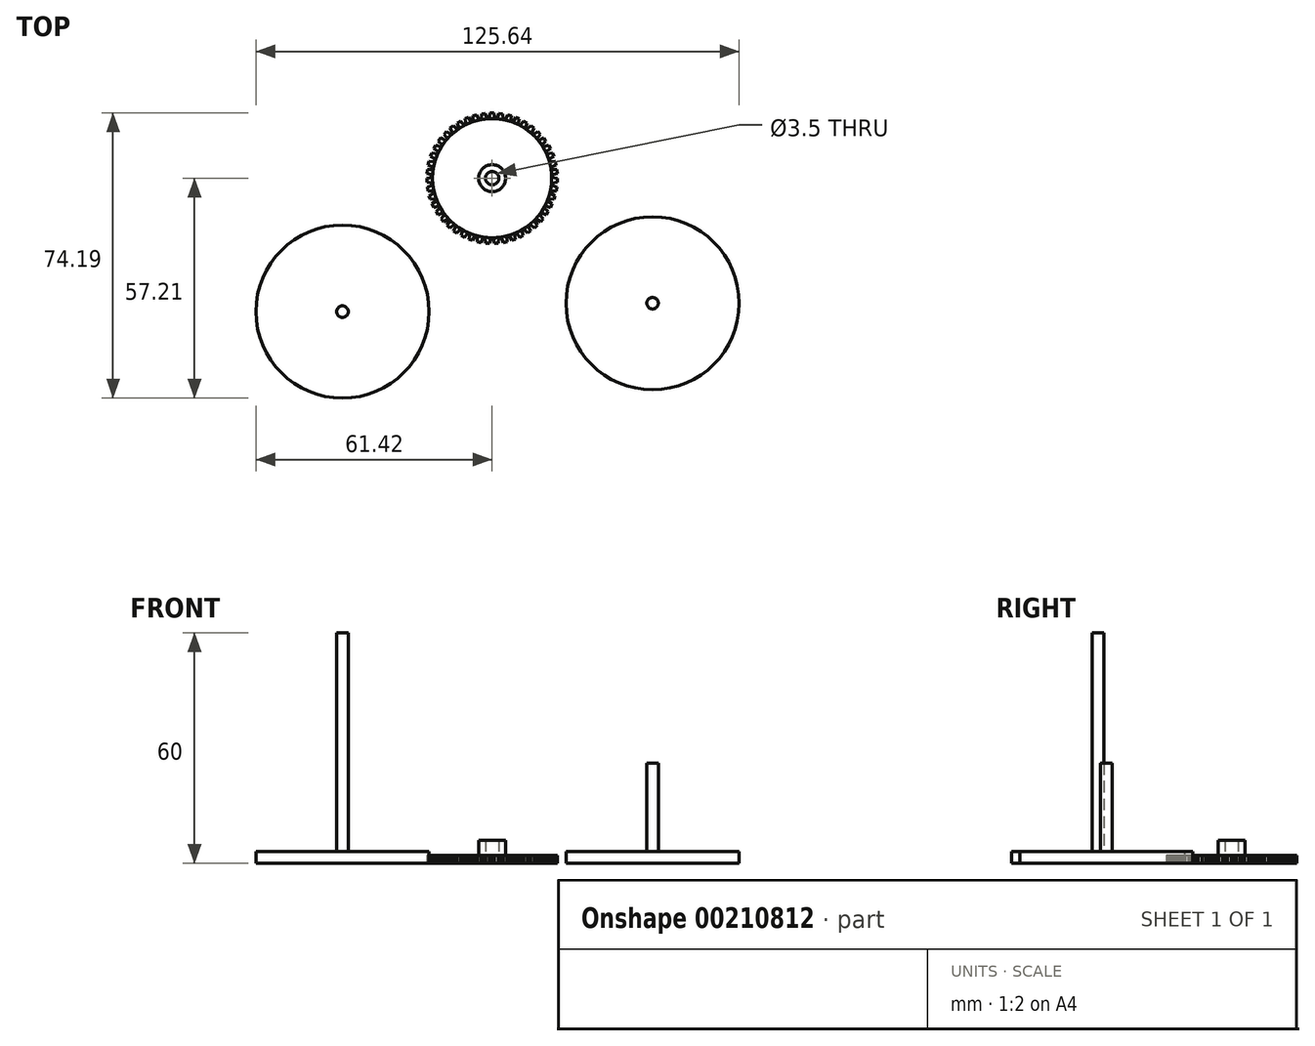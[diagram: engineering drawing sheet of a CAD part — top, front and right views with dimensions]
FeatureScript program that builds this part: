
annotation { "Feature Type Name" : "Feature", "Feature Type Description" : "" }
export const myFeature = defineFeature(function(context is Context, id is Id, definition is map)
    precondition{}
    {
        {
            var Q0;
            Q0=qCreatedBy(makeId("Top.planeOp"),FACE);
            var sketch = newSketch(context, id + "F0", { "sketchPlane" : qUnion([Q0])});
            skCircle(sketch, "E0", {"center": v(0, 0) * mm, "radius": 15.5 * mm});
            skLineSegment(sketch, "E1", {"start": v(-0.75, 15.48) * mm, "end": v(-0.5, 16.98) * mm});
            skLineSegment(sketch, "E2", {"start": v(-0.5, 16.98) * mm, "end": v(0.5, 16.98) * mm});
            skLineSegment(sketch, "E3", {"start": v(0.5, 16.98) * mm, "end": v(0.75, 15.48) * mm});
            skCircle(sketch, "E4", {"center": v(0, 0) * mm, "radius": 1.75 * mm});
            skCircle(sketch, "E5", {"center": v(0, 0) * mm, "radius": 3.5 * mm});
            skCircle(sketch, "E6", {"center": v(41.72, -32.53) * mm, "radius": 22.5 * mm});
            skCircle(sketch, "E7", {"center": v(41.72, -32.53) * mm, "radius": 1.5 * mm});
            skCircle(sketch, "E8", {"center": v(-38.92, -34.7) * mm, "radius": 22.5 * mm});
            skCircle(sketch, "E9", {"center": v(-38.92, -34.7) * mm, "radius": 1.5 * mm});
            skSolve(sketch);
        }
        {
            var Q0;
            {var subQ0=sQuery(id+"F0.wireOp",EDGE,"E0");var subQ1=makeQuery(id+"F0.imprint","INTERSECT",VERTEX,{"derivedFrom":[subQ0,sQuery(id+"F0.wireOp",EDGE,"E1")]});Q0=makeQuery(id+"F0.imprint","IMPRINT",FACE,{"disambiguationData":[TD([[makeQuery(id+"F0.imprint","IMPRINT",EDGE,{"disambiguationData":[TD([[subQ1,1.0]])],"derivedFrom":subQ0}),1.0]])]});}
            extrude(context, id + "F1", {"entities" : qUnion([Q0]), "depth" : 2 * mm});
        }
        {
            var Q0;
            {var subQ0=sQuery(id+"F0.wireOp",EDGE,"E1");Q0=makeQuery(id+"F0.imprint","IMPRINT",FACE,{"disambiguationData":[TD([[makeQuery(id+"F0.imprint","IMPRINT",EDGE,{"derivedFrom":subQ0}),-1.0]])]});}
            extrude(context, id + "F2", {"entities" : qUnion([Q0]), "depth" : 2 * mm});
        }
        {
            var Q0;
            Q0=makeQuery(id+"F2.opExtrude","SWEPT_BODY",BODY,{"disambiguationData":[OSD([sQuery(id+"F0.wireOp",EDGE,"E0"),sQuery(id+"F0.wireOp",EDGE,"E1"),sQuery(id+"F0.wireOp",EDGE,"E2"),sQuery(id+"F0.wireOp",EDGE,"E3")])]});
            var Q1;
            Q1=makeQuery(id+"F1.opExtrude","CAP_EDGE",EDGE,{"disambiguationData":[OSD([sQuery(id+"F0.wireOp",EDGE,"E0")])],"isStart":false});
            circularPattern(context, id + "F3", {"entities" : qUnion([Q0]), "axis" : qUnion([Q1]), "angle" : 360 * degree, "instanceCount" : 47, "equalSpace" : true});
        }
        {
            var Q0;
            Q0=makeQuery(id+"F0.imprint","IMPRINT",FACE,{"disambiguationData":[TD([[makeQuery(id+"F0.imprint","IMPRINT",EDGE,{"derivedFrom":sQuery(id+"F0.wireOp",EDGE,"E4")}),-1.0]])]});
            extrude(context, id + "F4", {"entities" : qUnion([Q0]), "operationType" : NewBodyOperationType.ADD, "depth" : 6 * mm});
        }
        {
            var Q0;
            Q0=makeQuery(id+"F0.imprint","IMPRINT",FACE,{"disambiguationData":[TD([[makeQuery(id+"F0.imprint","IMPRINT",EDGE,{"derivedFrom":sQuery(id+"F0.wireOp",EDGE,"E7")}),1.0]])]});
            extrude(context, id + "F5", {"entities" : qUnion([Q0]), "depth" : 26 * mm});
        }
        {
            var Q0;
            Q0=makeQuery(id+"F0.imprint","IMPRINT",FACE,{"disambiguationData":[TD([[makeQuery(id+"F0.imprint","IMPRINT",EDGE,{"derivedFrom":sQuery(id+"F0.wireOp",EDGE,"E6")}),1.0]])]});
            var Q1;
            Q1=makeQuery(id+"F0.imprint","IMPRINT",FACE,{"disambiguationData":[TD([[makeQuery(id+"F0.imprint","IMPRINT",EDGE,{"derivedFrom":sQuery(id+"F0.wireOp",EDGE,"E8")}),1.0]])]});
            extrude(context, id + "F6", {"entities" : qUnion([Q0, Q1]), "operationType" : NewBodyOperationType.ADD, "depth" : 3 * mm});
        }
        {
            var Q0;
            Q0=makeQuery(id+"F0.imprint","IMPRINT",FACE,{"disambiguationData":[TD([[makeQuery(id+"F0.imprint","IMPRINT",EDGE,{"derivedFrom":sQuery(id+"F0.wireOp",EDGE,"E9")}),1.0]])]});
            extrude(context, id + "F7", {"entities" : qUnion([Q0]), "operationType" : NewBodyOperationType.ADD, "depth" : 60 * mm});
        }
    });
